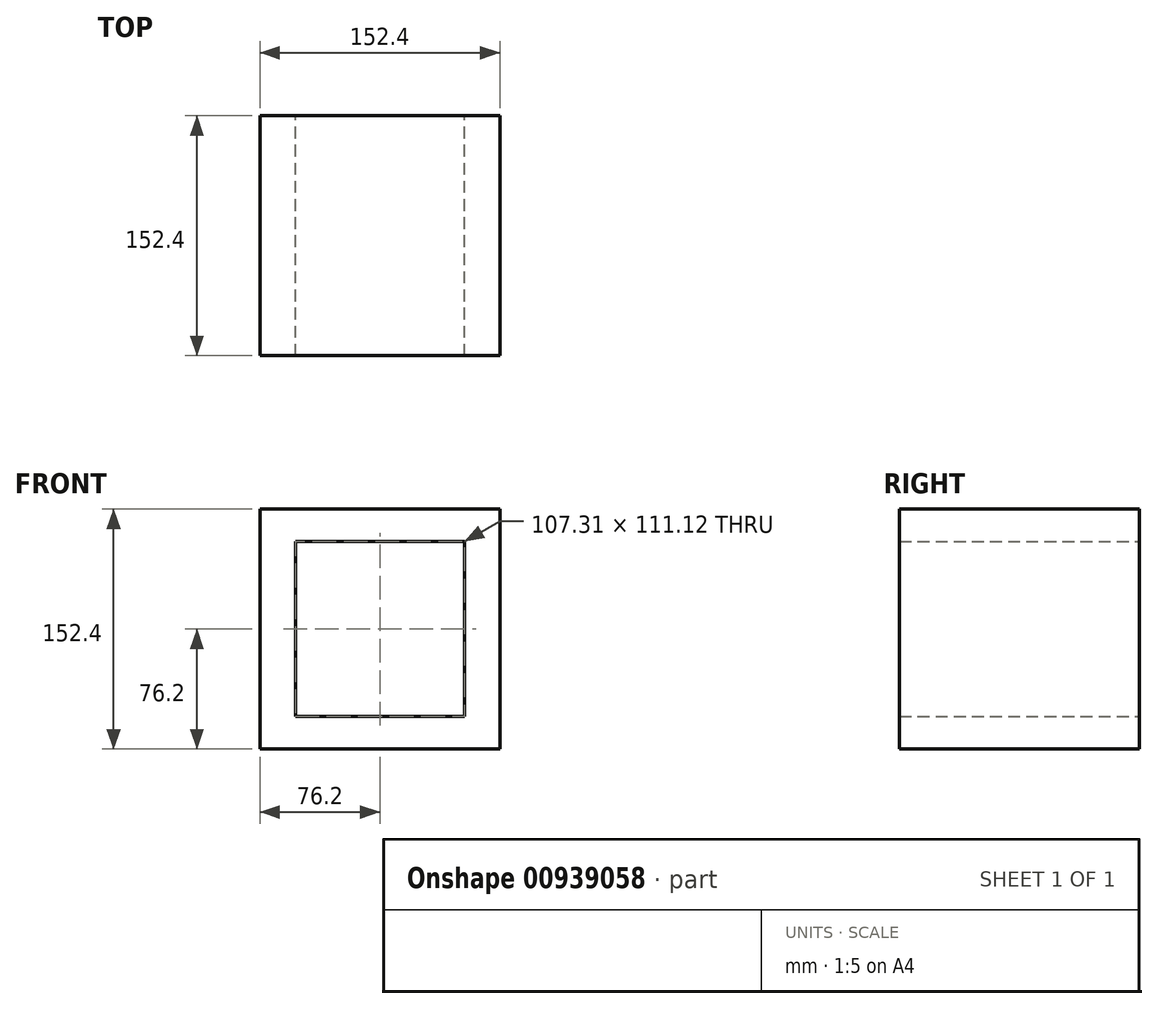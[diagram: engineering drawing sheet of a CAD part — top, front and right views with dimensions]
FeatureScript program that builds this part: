
annotation { "Feature Type Name" : "Feature", "Feature Type Description" : "" }
export const myFeature = defineFeature(function(context is Context, id is Id, definition is map)
    precondition{}
    {
        {
            var Q0;
            Q0=qCreatedBy(makeId("Front.planeOp"),FACE);
            var sketch = newSketch(context, id + "F0", { "sketchPlane" : qUnion([Q0])});
            skLineSegment(sketch, "E0.bottom", {"start": v(76.2, 76.2) * mm, "end": v(-76.2, 76.2) * mm});
            skLineSegment(sketch, "E0.top", {"start": v(76.2, -76.2) * mm, "end": v(-76.2, -76.2) * mm});
            skLineSegment(sketch, "E0.left", {"start": v(76.2, 76.2) * mm, "end": v(76.2, -76.2) * mm});
            skLineSegment(sketch, "E0.right", {"start": v(-76.2, 76.2) * mm, "end": v(-76.2, -76.2) * mm});
            skPoint(sketch, "E0.middle", {"position": v(0, 0) * mm});
            skLineSegment(sketch, "E1.bottom", {"start": v(53.66, 55.56) * mm, "end": v(-53.66, 55.56) * mm});
            skLineSegment(sketch, "E1.top", {"start": v(53.66, -55.56) * mm, "end": v(-53.66, -55.56) * mm});
            skLineSegment(sketch, "E1.left", {"start": v(53.66, 55.56) * mm, "end": v(53.66, -55.56) * mm});
            skLineSegment(sketch, "E1.right", {"start": v(-53.66, 55.56) * mm, "end": v(-53.66, -55.56) * mm});
            skSolve(sketch);
        }
        {
            var Q0;
            Q0=makeQuery(id+"F0.imprint","IMPRINT",FACE,{"disambiguationData":[TD([[makeQuery(id+"F0.imprint","IMPRINT",EDGE,{"derivedFrom":sQuery(id+"F0.wireOp",EDGE,"E0.bottom")}),1.0]])]});
            extrude(context, id + "F1", {"entities" : qUnion([Q0]), "depth" : 152.4 * mm, "offsetDistance" : 25.4 * mm});
        }
    });
